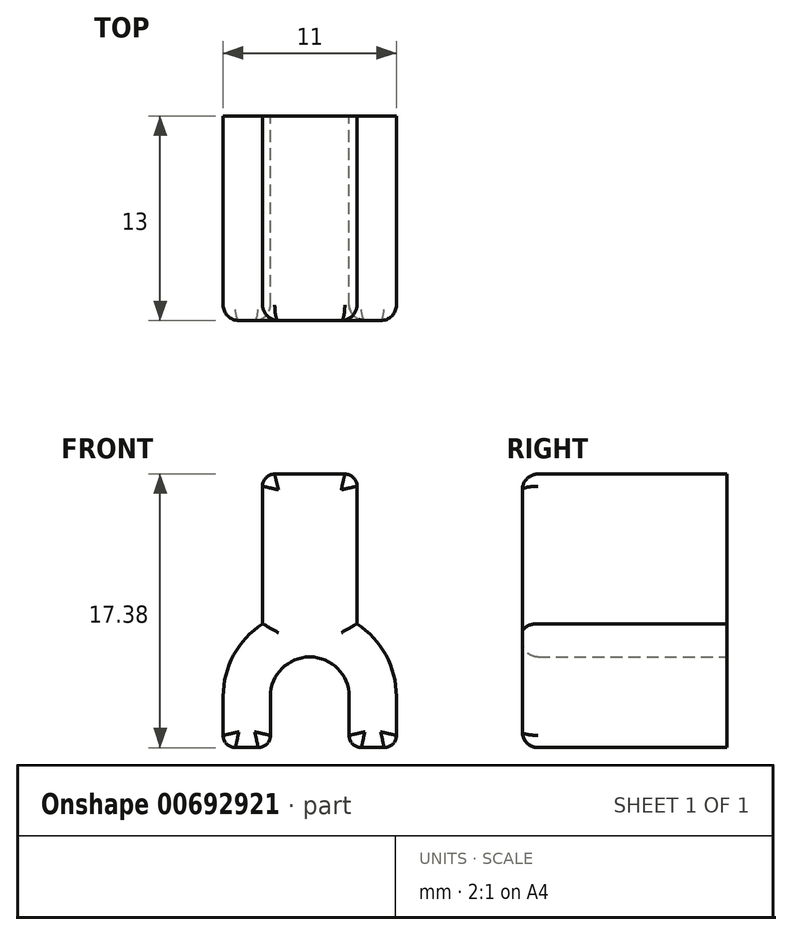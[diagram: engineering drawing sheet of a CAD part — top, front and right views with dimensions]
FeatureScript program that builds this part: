
annotation { "Feature Type Name" : "Feature", "Feature Type Description" : "" }
export const myFeature = defineFeature(function(context is Context, id is Id, definition is map)
    precondition{}
    {
        {
            var Q0;
            Q0=qCreatedBy(makeId("Front.planeOp"),FACE);
            var sketch = newSketch(context, id + "F0", { "sketchPlane" : qUnion([Q0])});
            skArc(sketch, "E0", {"start": v(2.5, -4.6) * mm, "mid": v(0, -2.1) * mm, "end": v(-2.5, -4.6) * mm});
            skLineSegment(sketch, "E1", {"start": v(2.5, -4.6) * mm, "end": v(2.5, -7.1) * mm});
            skLineSegment(sketch, "E2", {"start": v(3.27, -7.87) * mm, "end": v(4.73, -7.87) * mm});
            skLineSegment(sketch, "E3", {"start": v(-2.5, -4.6) * mm, "end": v(-2.5, -7.1) * mm});
            skLineSegment(sketch, "E4", {"start": v(-3.27, -7.87) * mm, "end": v(-4.73, -7.87) * mm});
            skLineSegment(sketch, "E5", {"start": v(5.5, -4.6) * mm, "end": v(5.5, -7.1) * mm});
            skLineSegment(sketch, "E6.top", {"start": v(-2.23, 9.5) * mm, "end": v(2.23, 9.5) * mm});
            skLineSegment(sketch, "E6.left", {"start": v(-3, 0) * mm, "end": v(-3, 8.73) * mm});
            skLineSegment(sketch, "E6.right", {"start": v(3, 0) * mm, "end": v(3, 8.73) * mm});
            skLineSegment(sketch, "E7", {"start": v(-5.5, -7.1) * mm, "end": v(-5.5, -4.6) * mm});
            skArc(sketch, "E8", {"start": v(5.5, -4.6) * mm, "mid": v(4.83, -1.99) * mm, "end": v(3, 0) * mm});
            skPoint(sketch, "E9.visualSharp", {"position": v(5.5, -7.87) * mm});
            skArc(sketch, "E9.filletArc", {"start": v(4.73, -7.87) * mm, "mid": v(5.27, -7.64) * mm, "end": v(5.5, -7.1) * mm});
            skPoint(sketch, "E10.visualSharp", {"position": v(2.5, -7.87) * mm});
            skArc(sketch, "E10.filletArc", {"start": v(2.5, -7.1) * mm, "mid": v(2.73, -7.64) * mm, "end": v(3.27, -7.87) * mm});
            skPoint(sketch, "E11.visualSharp", {"position": v(-2.5, -7.87) * mm});
            skArc(sketch, "E11.filletArc", {"start": v(-3.27, -7.87) * mm, "mid": v(-2.73, -7.64) * mm, "end": v(-2.5, -7.1) * mm});
            skPoint(sketch, "E12.visualSharp", {"position": v(-5.5, -7.87) * mm});
            skArc(sketch, "E12.filletArc", {"start": v(-5.5, -7.1) * mm, "mid": v(-5.27, -7.64) * mm, "end": v(-4.73, -7.87) * mm});
            skPoint(sketch, "E13.visualSharp", {"position": v(3, 9.5) * mm});
            skArc(sketch, "E13.filletArc", {"start": v(3, 8.73) * mm, "mid": v(2.77, 9.28) * mm, "end": v(2.23, 9.5) * mm});
            skPoint(sketch, "E14.visualSharp", {"position": v(-3, 9.5) * mm});
            skArc(sketch, "E14.filletArc", {"start": v(-2.23, 9.5) * mm, "mid": v(-2.77, 9.28) * mm, "end": v(-3, 8.73) * mm});
            skArc(sketch, "E15.trimOffspring", {"start": v(-3, 0) * mm, "mid": v(-4.83, -1.99) * mm, "end": v(-5.5, -4.6) * mm});
            skSolve(sketch);
        }
        {
            var Q0;
            Q0=makeQuery(id+"F0.imprint","IMPRINT",FACE,{"disambiguationData":[TD([[makeQuery(id+"F0.imprint","IMPRINT",EDGE,{"derivedFrom":sQuery(id+"F0.wireOp",EDGE,"WPMeiH55-fet9-0iw4-tUZo-IH2l8WZ0b3oq.left")}),1.0]])]});
            var Q1;
            Q1=makeQuery(id+"F0.imprint","IMPRINT",FACE,{"disambiguationData":[TD([[makeQuery(id+"F0.imprint","IMPRINT",EDGE,{"derivedFrom":sQuery(id+"F0.wireOp",EDGE,"E6.top")}),-1.0]])]});
            extrude(context, id + "F1", {"entities" : qUnion([Q0, Q1]), "depth" : 13 * mm, "offsetDistance" : 25 * mm});
        }
        {
            var Q0;
            Q0=makeQuery(id+"F1.opExtrude","CAP_EDGE",EDGE,{"disambiguationData":[OSD([sQuery(id+"F0.wireOp",EDGE,"E6.left")])],"isStart":false});
            var Q1;
            Q1=makeQuery(id+"F1.opExtrude","CAP_EDGE",EDGE,{"disambiguationData":[OSD([sQuery(id+"F0.wireOp",EDGE,"E15.trimOffspring")])],"isStart":false});
            fillet(context, id + "F2", {"entities" : qUnion([Q0, Q1]), "radius" : 1 * mm, "tangentPropagation" : true, "allowEdgeOverflow" : false});
        }
    });
